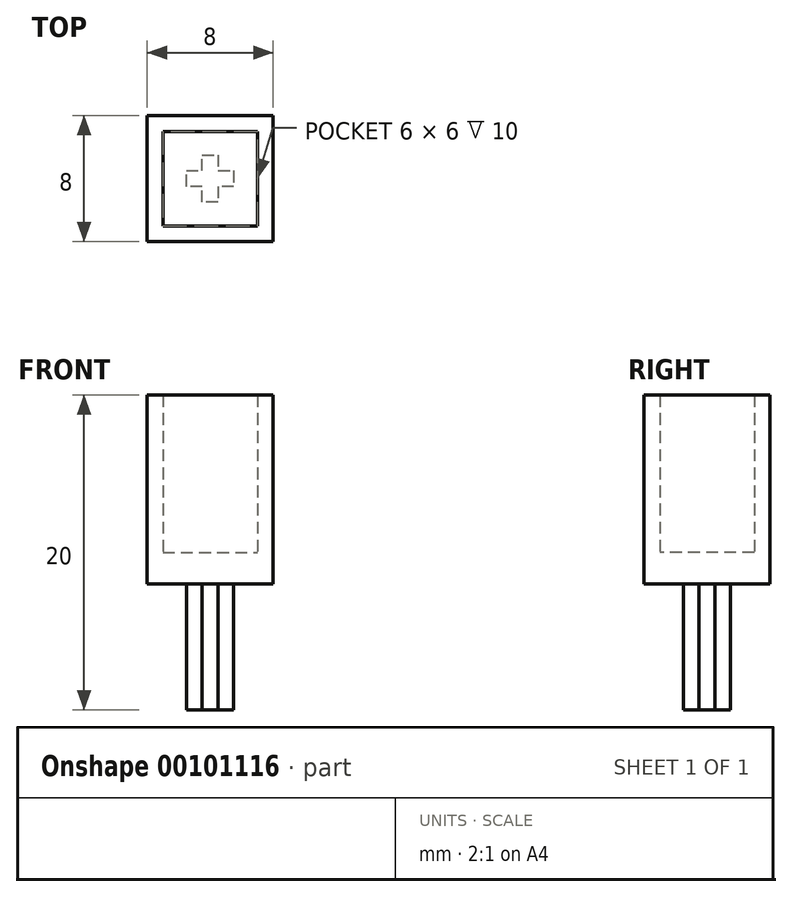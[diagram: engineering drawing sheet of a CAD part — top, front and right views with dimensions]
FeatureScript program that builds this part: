
annotation { "Feature Type Name" : "Feature", "Feature Type Description" : "" }
export const myFeature = defineFeature(function(context is Context, id is Id, definition is map)
    precondition{}
    {
        {
            var Q0;
            Q0=qCreatedBy(makeId("Top.planeOp"),FACE);
            var sketch = newSketch(context, id + "F0", { "sketchPlane" : qUnion([Q0])});
            skLineSegment(sketch, "E0", {"start": v(-1.5, 0.5) * mm, "end": v(-0.5, 0.5) * mm});
            skLineSegment(sketch, "E1", {"start": v(-0.5, 0.5) * mm, "end": v(-0.5, 1.5) * mm});
            skLineSegment(sketch, "E2", {"start": v(-0.5, 1.5) * mm, "end": v(0.5, 1.5) * mm});
            skLineSegment(sketch, "E3", {"start": v(0.5, 1.5) * mm, "end": v(0.5, 0.5) * mm});
            skLineSegment(sketch, "E4", {"start": v(0.5, 0.5) * mm, "end": v(1.5, 0.5) * mm});
            skLineSegment(sketch, "E5", {"start": v(1.5, 0.5) * mm, "end": v(1.5, -0.5) * mm});
            skLineSegment(sketch, "E6", {"start": v(1.5, -0.5) * mm, "end": v(0.5, -0.5) * mm});
            skLineSegment(sketch, "E7", {"start": v(0.5, -0.5) * mm, "end": v(0.5, -1.5) * mm});
            skLineSegment(sketch, "E8", {"start": v(0.5, -1.5) * mm, "end": v(-0.5, -1.5) * mm});
            skLineSegment(sketch, "E9", {"start": v(-0.5, -1.5) * mm, "end": v(-0.5, -0.5) * mm});
            skLineSegment(sketch, "E10", {"start": v(-0.5, -0.5) * mm, "end": v(-1.5, -0.5) * mm});
            skLineSegment(sketch, "E11", {"start": v(-1.5, -0.5) * mm, "end": v(-1.5, 0.5) * mm});
            skPoint(sketch, "E12", {"position": v(-1.5, 0) * mm});
            skPoint(sketch, "E13", {"position": v(0, 1.5) * mm});
            skSolve(sketch);
        }
        {
            var Q0;
            Q0=makeQuery(id+"F0.imprint","IMPRINT",FACE,{"disambiguationData":[TD([[makeQuery(id+"F0.imprint","IMPRINT",EDGE,{"derivedFrom":sQuery(id+"F0.wireOp",EDGE,"E0")}),-1.0]])]});
            extrude(context, id + "F1", {"entities" : qUnion([Q0]), "depth" : 10 * mm});
        }
        {
            var Q0;
            Q0=makeQuery(id+"F1.opExtrude","CAP_FACE",FACE,{"disambiguationData":[OSD([sQuery(id+"F0.wireOp",EDGE,"E0"),sQuery(id+"F0.wireOp",EDGE,"E1"),sQuery(id+"F0.wireOp",EDGE,"E2"),sQuery(id+"F0.wireOp",EDGE,"E3"),sQuery(id+"F0.wireOp",EDGE,"E4"),sQuery(id+"F0.wireOp",EDGE,"E5"),sQuery(id+"F0.wireOp",EDGE,"E6"),sQuery(id+"F0.wireOp",EDGE,"E7"),sQuery(id+"F0.wireOp",EDGE,"E8"),sQuery(id+"F0.wireOp",EDGE,"E9"),sQuery(id+"F0.wireOp",EDGE,"E10"),sQuery(id+"F0.wireOp",EDGE,"E11")])],"isStart":false});
            var sketch = newSketch(context, id + "F2", { "sketchPlane" : qUnion([Q0])});
            skLineSegment(sketch, "E14.bottom", {"start": v(-4, 4) * mm, "end": v(4, 4) * mm});
            skLineSegment(sketch, "E14.top", {"start": v(-4, -4) * mm, "end": v(4, -4) * mm});
            skLineSegment(sketch, "E14.left", {"start": v(-4, 4) * mm, "end": v(-4, -4) * mm});
            skLineSegment(sketch, "E14.right", {"start": v(4, 4) * mm, "end": v(4, -4) * mm});
            skPoint(sketch, "E14.middle", {"position": v(0, 0) * mm});
            skLineSegment(sketch, "E15.bottom", {"start": v(-3, 3) * mm, "end": v(3, 3) * mm});
            skLineSegment(sketch, "E15.top", {"start": v(-3, -3) * mm, "end": v(3, -3) * mm});
            skLineSegment(sketch, "E15.left", {"start": v(-3, 3) * mm, "end": v(-3, -3) * mm});
            skLineSegment(sketch, "E15.right", {"start": v(3, 3) * mm, "end": v(3, -3) * mm});
            skSolve(sketch);
        }
        {
            var Q0;
            {var subQ0=sQuery(id+"F2.wireOp",EDGE,"E15.right");var subQ1=sQuery(id+"F2.wireOp",EDGE,"E15.bottom");var subQ2=makeQuery(id+"F2.imprint","INTERSECT",VERTEX,{"derivedFrom":[subQ1,subQ0]});Q0=makeQuery(id+"F2.imprint","IMPRINT",FACE,{"disambiguationData":[TD([[makeQuery(id+"F2.imprint","IMPRINT",EDGE,{"disambiguationData":[TD([[subQ2,1.0]])],"derivedFrom":subQ1}),-1.0]])]});}
            var Q1;
            Q1=makeQuery(id+"F2.imprint","IMPRINT",FACE,{"disambiguationData":[TD([[makeQuery(id+"F2.imprint","IMPRINT",EDGE,{"derivedFrom":sQuery(id+"F2.wireOp",EDGE,"E14.bottom")}),-1.0]])]});
            var Q2;
            {var subQ0=sQuery(id+"F2.wireOp",EDGE,"E15.left");var subQ1=sQuery(id+"F2.wireOp",EDGE,"E15.bottom");var subQ2=makeQuery(id+"F2.imprint","INTERSECT",VERTEX,{"derivedFrom":[subQ1,subQ0]});Q2=makeQuery(id+"F2.imprint","IMPRINT",FACE,{"disambiguationData":[TD([[makeQuery(id+"F2.imprint","IMPRINT",EDGE,{"disambiguationData":[TD([[subQ2,-1.0]])],"derivedFrom":subQ1}),-1.0]])]});}
            var Q3;
            {var subQ0=sQuery(id+"F2.wireOp",EDGE,"E15.left");var subQ1=sQuery(id+"F2.wireOp",EDGE,"E15.top");var subQ2=makeQuery(id+"F2.imprint","INTERSECT",VERTEX,{"derivedFrom":[subQ1,subQ0]});Q3=makeQuery(id+"F2.imprint","IMPRINT",FACE,{"disambiguationData":[TD([[makeQuery(id+"F2.imprint","IMPRINT",EDGE,{"disambiguationData":[TD([[subQ2,-1.0]])],"derivedFrom":subQ1}),1.0]])]});}
            var Q4;
            {var subQ0=sQuery(id+"F2.wireOp",EDGE,"E15.right");var subQ1=sQuery(id+"F2.wireOp",EDGE,"E15.top");var subQ2=makeQuery(id+"F2.imprint","INTERSECT",VERTEX,{"derivedFrom":[subQ1,subQ0]});Q4=makeQuery(id+"F2.imprint","IMPRINT",FACE,{"disambiguationData":[TD([[makeQuery(id+"F2.imprint","IMPRINT",EDGE,{"disambiguationData":[TD([[subQ2,1.0]])],"derivedFrom":subQ1}),1.0]])]});}
            extrude(context, id + "F3", {"entities" : qUnion([Q0, Q1, Q2, Q3, Q4]), "operationType" : NewBodyOperationType.ADD, "oppositeDirection" : true, "depth" : 2 * mm});
        }
        {
            var Q0;
            Q0=makeQuery(id+"F2.imprint","IMPRINT",FACE,{"disambiguationData":[TD([[makeQuery(id+"F2.imprint","IMPRINT",EDGE,{"derivedFrom":sQuery(id+"F2.wireOp",EDGE,"E14.bottom")}),-1.0]])]});
            extrude(context, id + "F4", {"entities" : qUnion([Q0]), "operationType" : NewBodyOperationType.ADD, "depth" : 10 * mm});
        }
    });
